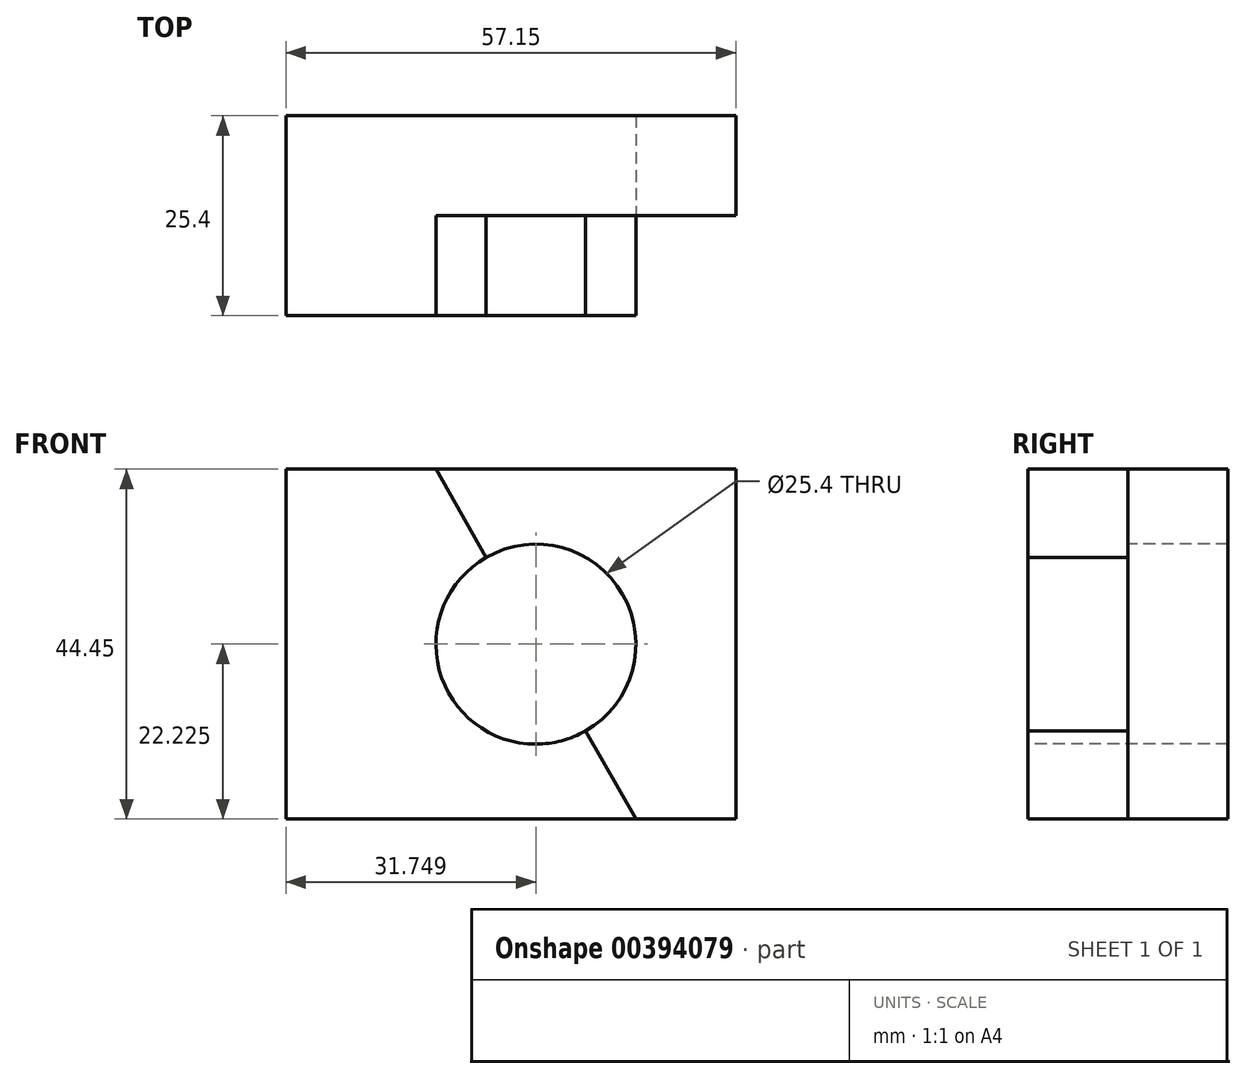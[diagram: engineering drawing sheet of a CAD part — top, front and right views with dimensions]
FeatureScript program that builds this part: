
annotation { "Feature Type Name" : "Feature", "Feature Type Description" : "" }
export const myFeature = defineFeature(function(context is Context, id is Id, definition is map)
    precondition{}
    {
        {
            var Q0;
            Q0=qCreatedBy(makeId("Front.planeOp"),FACE);
            var sketch = newSketch(context, id + "F0", { "sketchPlane" : qUnion([Q0])});
            skLineSegment(sketch, "E0", {"start": v(-53.84, 44.45) * mm, "end": v(-53.84, 0) * mm});
            skLineSegment(sketch, "E1", {"start": v(-53.84, 0) * mm, "end": v(3.3, 0) * mm});
            skLineSegment(sketch, "E2", {"start": v(3.3, 0) * mm, "end": v(3.3, 44.45) * mm});
            skLineSegment(sketch, "E3", {"start": v(3.3, 44.45) * mm, "end": v(-53.84, 44.45) * mm});
            skSolve(sketch);
        }
        {
            var Q0;
            Q0=makeQuery(id+"F0.imprint","IMPRINT",FACE,{"disambiguationData":[TD([[makeQuery(id+"F0.imprint","IMPRINT",EDGE,{"derivedFrom":sQuery(id+"F0.wireOp",EDGE,"E0")}),1.0]])]});
            extrude(context, id + "F1", {"entities" : qUnion([Q0]), "depth" : 25.4 * mm});
        }
        {
            var Q0;
            Q0=makeQuery(id+"F1.opExtrude","CAP_FACE",FACE,{"disambiguationData":[OSD([sQuery(id+"F0.wireOp",EDGE,"E0"),sQuery(id+"F0.wireOp",EDGE,"E1"),sQuery(id+"F0.wireOp",EDGE,"E2"),sQuery(id+"F0.wireOp",EDGE,"E3")])],"isStart":false});
            var sketch = newSketch(context, id + "F2", { "sketchPlane" : qUnion([Q0])});
            skLineSegment(sketch, "E4", {"start": v(-34.8, 44.45) * mm, "end": v(-9.4, 0) * mm});
            skSolve(sketch);
        }
        {
            var Q0;
            {var subQ0=sQuery(id+"F2.wireOp",EDGE,"E4");Q0=makeQuery(id+"F2.imprint","IMPRINT",FACE,{"disambiguationData":[TD([[makeQuery(id+"F2.imprint","IMPRINT",EDGE,{"derivedFrom":subQ0}),1.0]])]});}
            extrude(context, id + "F3", {"entities" : qUnion([Q0]), "operationType" : NewBodyOperationType.REMOVE, "oppositeDirection" : true, "depth" : 12.7 * mm});
        }
        {
            var Q0;
            Q0=makeQuery(id+"F1.opExtrude","CAP_FACE",FACE,{"disambiguationData":[OSD([sQuery(id+"F0.wireOp",EDGE,"E0"),sQuery(id+"F0.wireOp",EDGE,"E1"),sQuery(id+"F0.wireOp",EDGE,"E2"),sQuery(id+"F0.wireOp",EDGE,"E3")])],"isStart":false});
            var sketch = newSketch(context, id + "F4", { "sketchPlane" : qUnion([Q0])});
            skCircle(sketch, "E5", {"center": v(-22.1, 22.23) * mm, "radius": 12.7 * mm});
            skSolve(sketch);
        }
        {
            var Q0;
            {var subQ0=sQuery(id+"F4.wireOp",EDGE,"E5");var subQ1=makeQuery(id+"F3.boolean.opBoolean","COPY",EDGE,{"derivedFrom":makeQuery(id+"F3.opExtrude","CAP_EDGE",EDGE,{"disambiguationData":[OSD([sQuery(id+"F2.wireOp",EDGE,"E4")])],"isStart":true})});var subQ2=makeQuery(id+"F4.imprint","INTERSECT",VERTEX,{"disambiguationData":[OD(0.0)],"derivedFrom":[subQ1,subQ0]});Q0=makeQuery(id+"F4.imprint","IMPRINT",FACE,{"disambiguationData":[TD([[makeQuery(id+"F4.imprint","IMPRINT",EDGE,{"disambiguationData":[TD([[subQ2,-1.0]])],"derivedFrom":subQ0}),1.0]])]});}
            var Q1;
            {var subQ0=sQuery(id+"F4.wireOp",EDGE,"E5");var subQ1=makeQuery(id+"F3.boolean.opBoolean","COPY",EDGE,{"derivedFrom":makeQuery(id+"F3.opExtrude","CAP_EDGE",EDGE,{"disambiguationData":[OSD([sQuery(id+"F2.wireOp",EDGE,"E4")])],"isStart":true})});var subQ2=makeQuery(id+"F4.imprint","INTERSECT",VERTEX,{"disambiguationData":[OD(0.0)],"derivedFrom":[subQ1,subQ0]});Q1=makeQuery(id+"F4.imprint","IMPRINT",FACE,{"disambiguationData":[TD([[makeQuery(id+"F4.imprint","IMPRINT",EDGE,{"disambiguationData":[TD([[subQ2,1.0]])],"derivedFrom":subQ0}),1.0]])]});}
            extrude(context, id + "F5", {"entities" : qUnion([Q0, Q1]), "operationType" : NewBodyOperationType.REMOVE, "oppositeDirection" : true, "depth" : 25.4 * mm});
        }
    });
